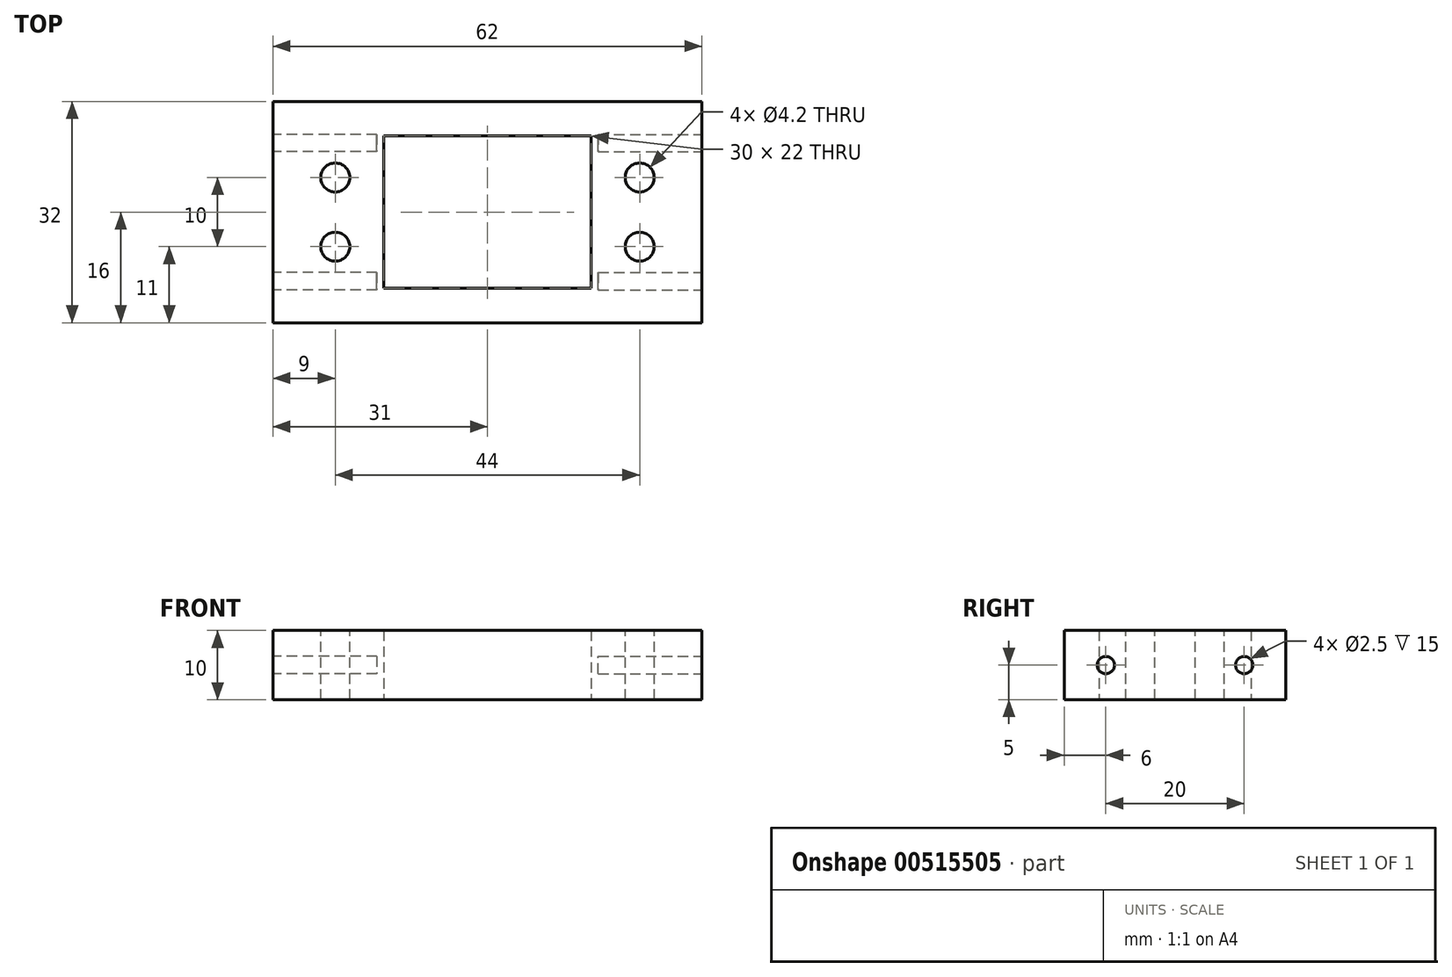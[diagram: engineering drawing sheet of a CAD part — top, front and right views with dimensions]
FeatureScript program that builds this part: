
annotation { "Feature Type Name" : "Feature", "Feature Type Description" : "" }
export const myFeature = defineFeature(function(context is Context, id is Id, definition is map)
    precondition{}
    {
        {
            var Q0;
            Q0=qCreatedBy(makeId("Top.planeOp"),FACE);
            var sketch = newSketch(context, id + "F0", { "sketchPlane" : qUnion([Q0])});
            skLineSegment(sketch, "E0.bottom", {"start": v(31, -16) * mm, "end": v(-31, -16) * mm});
            skLineSegment(sketch, "E0.top", {"start": v(31, 16) * mm, "end": v(-31, 16) * mm});
            skLineSegment(sketch, "E0.left", {"start": v(31, -16) * mm, "end": v(31, 16) * mm});
            skLineSegment(sketch, "E0.right", {"start": v(-31, -16) * mm, "end": v(-31, 16) * mm});
            skPoint(sketch, "E0.middle", {"position": v(0, 0) * mm});
            skLineSegment(sketch, "E1.bottom", {"start": v(15, -11) * mm, "end": v(-15, -11) * mm});
            skLineSegment(sketch, "E1.top", {"start": v(15, 11) * mm, "end": v(-15, 11) * mm});
            skLineSegment(sketch, "E1.left", {"start": v(15, -11) * mm, "end": v(15, 11) * mm});
            skLineSegment(sketch, "E1.right", {"start": v(-15, -11) * mm, "end": v(-15, 11) * mm});
            skSolve(sketch);
        }
        {
            var Q0;
            Q0=makeQuery(id+"F0.imprint","IMPRINT",FACE,{"disambiguationData":[TD([[makeQuery(id+"F0.imprint","IMPRINT",EDGE,{"derivedFrom":sQuery(id+"F0.wireOp",EDGE,"E0.bottom")}),-1.0]])]});
            extrude(context, id + "F1", {"entities" : qUnion([Q0]), "depth" : 10 * mm, "offsetDistance" : 25 * mm});
        }
        {
            var Q0;
            Q0=makeQuery(id+"F1.opExtrude","CAP_FACE",FACE,{"disambiguationData":[OSD([sQuery(id+"F0.wireOp",EDGE,"E0.bottom"),sQuery(id+"F0.wireOp",EDGE,"E0.top"),sQuery(id+"F0.wireOp",EDGE,"E0.left"),sQuery(id+"F0.wireOp",EDGE,"E0.right"),sQuery(id+"F0.wireOp",EDGE,"E1.bottom"),sQuery(id+"F0.wireOp",EDGE,"E1.top"),sQuery(id+"F0.wireOp",EDGE,"E1.left"),sQuery(id+"F0.wireOp",EDGE,"E1.right")])],"isStart":false});
            var sketch = newSketch(context, id + "F2", { "sketchPlane" : qUnion([Q0])});
            skCircle(sketch, "E2", {"center": v(22, 5) * mm, "radius": 2.1 * mm});
            skCircle(sketch, "E3", {"center": v(22, -5) * mm, "radius": 2.1 * mm});
            skCircle(sketch, "E4", {"center": v(-22, -5) * mm, "radius": 2.1 * mm});
            skCircle(sketch, "E5", {"center": v(-22, 5) * mm, "radius": 2.1 * mm});
            skSolve(sketch);
        }
        {
            var Q0;
            Q0=makeQuery(id+"F2.imprint","IMPRINT",FACE,{"disambiguationData":[TD([[makeQuery(id+"F2.imprint","IMPRINT",EDGE,{"derivedFrom":sQuery(id+"F2.wireOp",EDGE,"E5")}),1.0]])]});
            var Q1;
            Q1=makeQuery(id+"F2.imprint","IMPRINT",FACE,{"disambiguationData":[TD([[makeQuery(id+"F2.imprint","IMPRINT",EDGE,{"derivedFrom":sQuery(id+"F2.wireOp",EDGE,"E4")}),1.0]])]});
            var Q2;
            Q2=makeQuery(id+"F2.imprint","IMPRINT",FACE,{"disambiguationData":[TD([[makeQuery(id+"F2.imprint","IMPRINT",EDGE,{"derivedFrom":sQuery(id+"F2.wireOp",EDGE,"E2")}),1.0]])]});
            var Q3;
            Q3=makeQuery(id+"F2.imprint","IMPRINT",FACE,{"disambiguationData":[TD([[makeQuery(id+"F2.imprint","IMPRINT",EDGE,{"derivedFrom":sQuery(id+"F2.wireOp",EDGE,"E3")}),1.0]])]});
            extrude(context, id + "F3", {"entities" : qUnion([Q0, Q1, Q2, Q3]), "operationType" : NewBodyOperationType.REMOVE, "endBound" : BoundingType.THROUGH_ALL, "oppositeDirection" : true, "depth" : 25 * mm, "offsetDistance" : 25 * mm});
        }
        {
            var Q0;
            Q0=makeQuery(id+"F1.opExtrude","SWEPT_FACE",FACE,{"disambiguationData":[OSD([sQuery(id+"F0.wireOp",EDGE,"E0.left")])]});
            var sketch = newSketch(context, id + "F4", { "sketchPlane" : qUnion([Q0])});
            skCircle(sketch, "E6", {"center": v(10, 5) * mm, "radius": 1.25 * mm});
            skCircle(sketch, "E7", {"center": v(-10, 5) * mm, "radius": 1.25 * mm});
            skSolve(sketch);
        }
        {
            var Q0;
            Q0=makeQuery(id+"F4.imprint","IMPRINT",FACE,{"disambiguationData":[TD([[makeQuery(id+"F4.imprint","IMPRINT",EDGE,{"derivedFrom":sQuery(id+"F4.wireOp",EDGE,"E6")}),1.0]])]});
            var Q1;
            Q1=makeQuery(id+"F4.imprint","IMPRINT",FACE,{"disambiguationData":[TD([[makeQuery(id+"F4.imprint","IMPRINT",EDGE,{"derivedFrom":sQuery(id+"F4.wireOp",EDGE,"E7")}),1.0]])]});
            extrude(context, id + "F5", {"entities" : qUnion([Q0, Q1]), "operationType" : NewBodyOperationType.REMOVE, "oppositeDirection" : true, "depth" : 15 * mm, "offsetDistance" : 25 * mm});
        }
        {
            var Q0;
            Q0=makeQuery(id+"F1.opExtrude","SWEPT_FACE",FACE,{"disambiguationData":[OSD([sQuery(id+"F0.wireOp",EDGE,"E0.right")])]});
            var sketch = newSketch(context, id + "F6", { "sketchPlane" : qUnion([Q0])});
            skCircle(sketch, "E8", {"center": v(-10, 5) * mm, "radius": 1.25 * mm});
            skCircle(sketch, "E9", {"center": v(10, 5) * mm, "radius": 1.25 * mm});
            skSolve(sketch);
        }
        {
            var Q0;
            Q0=makeQuery(id+"F6.imprint","IMPRINT",FACE,{"disambiguationData":[TD([[makeQuery(id+"F6.imprint","IMPRINT",EDGE,{"derivedFrom":sQuery(id+"F6.wireOp",EDGE,"E8")}),1.0]])]});
            var Q1;
            Q1=makeQuery(id+"F6.imprint","IMPRINT",FACE,{"disambiguationData":[TD([[makeQuery(id+"F6.imprint","IMPRINT",EDGE,{"derivedFrom":sQuery(id+"F6.wireOp",EDGE,"E9")}),1.0]])]});
            extrude(context, id + "F7", {"entities" : qUnion([Q0, Q1]), "operationType" : NewBodyOperationType.REMOVE, "oppositeDirection" : true, "depth" : 15 * mm, "offsetDistance" : 25 * mm});
        }
    });
